# Revit family: GCD Garage Door
name_source: partatom
category: Doors
revit_build: Autodesk Revit 2017 (Build: 20170118_1100(x64)
units: mm (PartAtom-declared; Revit-internal decimal feet)

## family parameters
Always vertical = Yes
Cut with Voids When Loaded = No
Host = Wall
OmniClass Number = 23.30.10.00
OmniClass Title = Doors
Room Calculation Point = No
Shared = No

## types (2) — shared parameters
Analytic Construction = Metal
Assembly Code = B2030400
Frame Material = Steel, Paint Finish, Ivory, Matte
Function = Exterior
Heat Transfer Coefficient (U) = 0.652 BTU/(h·ft²·°F)
Height = 2438 mm
Manufacturer = CLOPAY
Panel Height = 610 mm
Panel Material = Steel, Paint Finish, Ivory, Matte
Panels = 4
Rough Height = 2464 mm
Thermal Resistance (R) = 1.5338 (h·ft²·°F)/BTU
Thickness = 38 mm
Trim Material = Steel, Paint Finish, Ivory, Matte
Wall Closure = By host
zero-valued in all types: Solar Heat Gain Coefficient, Visual Light Transmittance

## per-type parameters (varying)
| type | Description | Rough Width | Width |
| 16080 OHGD | 16080 OHGD | 4928 mm | 4877 mm |
| 9080 OHGD 2 | 9080 OHGD | 2794 mm  [stored 9.16667 ft] | 2743 mm |

note: [stored X ft] marks values corroborated as IEEE doubles in the binary element streams (Revit-internal decimal feet)

## geometry (parser evidence)
native form markers: Sweep x8
no freeform markers — native parametric forms only
